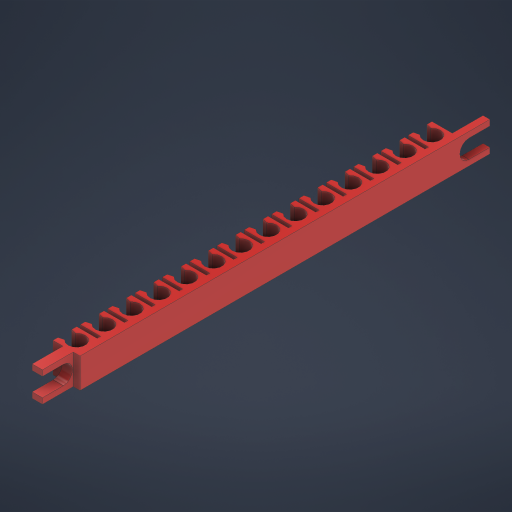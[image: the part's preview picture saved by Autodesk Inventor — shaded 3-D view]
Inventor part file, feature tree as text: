
AUTODESK INVENTOR PART (.ipt)
format: ipt  version: 2024 (Build 280153000, 153)  size: 436,224 bytes
history: native  units: in
note: dims shown in document units (in); Inventor stores cm internally (conversion verified against a paired STEP export)
features: extrude x2, sketch x2
ambient origin geometry x8: Origin, YZ Plane, XZ Plane, XY Plane, X Axis, Y Axis, Z Axis, Center Point
bodies: Solid1 (feature_tree)
feature tree (4):
  extrude  "Extrusion1"  Depth=0.2975in
  extrude  "Extrusion2"  Depth=0.125in
  sketch  "Sketch1"  dims[d1=0.2975in d5=0.7146in]
  sketch  "Sketch3"  dims[d6=0.7146in d7=0.125in d8=0.08in d9=0.1in d10=0.05in d11=0.35in d12=0.075in d14=5.5118in d16=0.4in d17=0.3937in d19=1.0in d21=0.4375in d22=0.0in d25=5.6in d26=2.8in d27=0.45in d28=0.15in d29=0.1in d41=0.45in d45=0.4375in d46=0.2188in d47=0.305in d48=0.305in d49=0.27in d50=0.27in d51=0.0in d52=0.0in]
